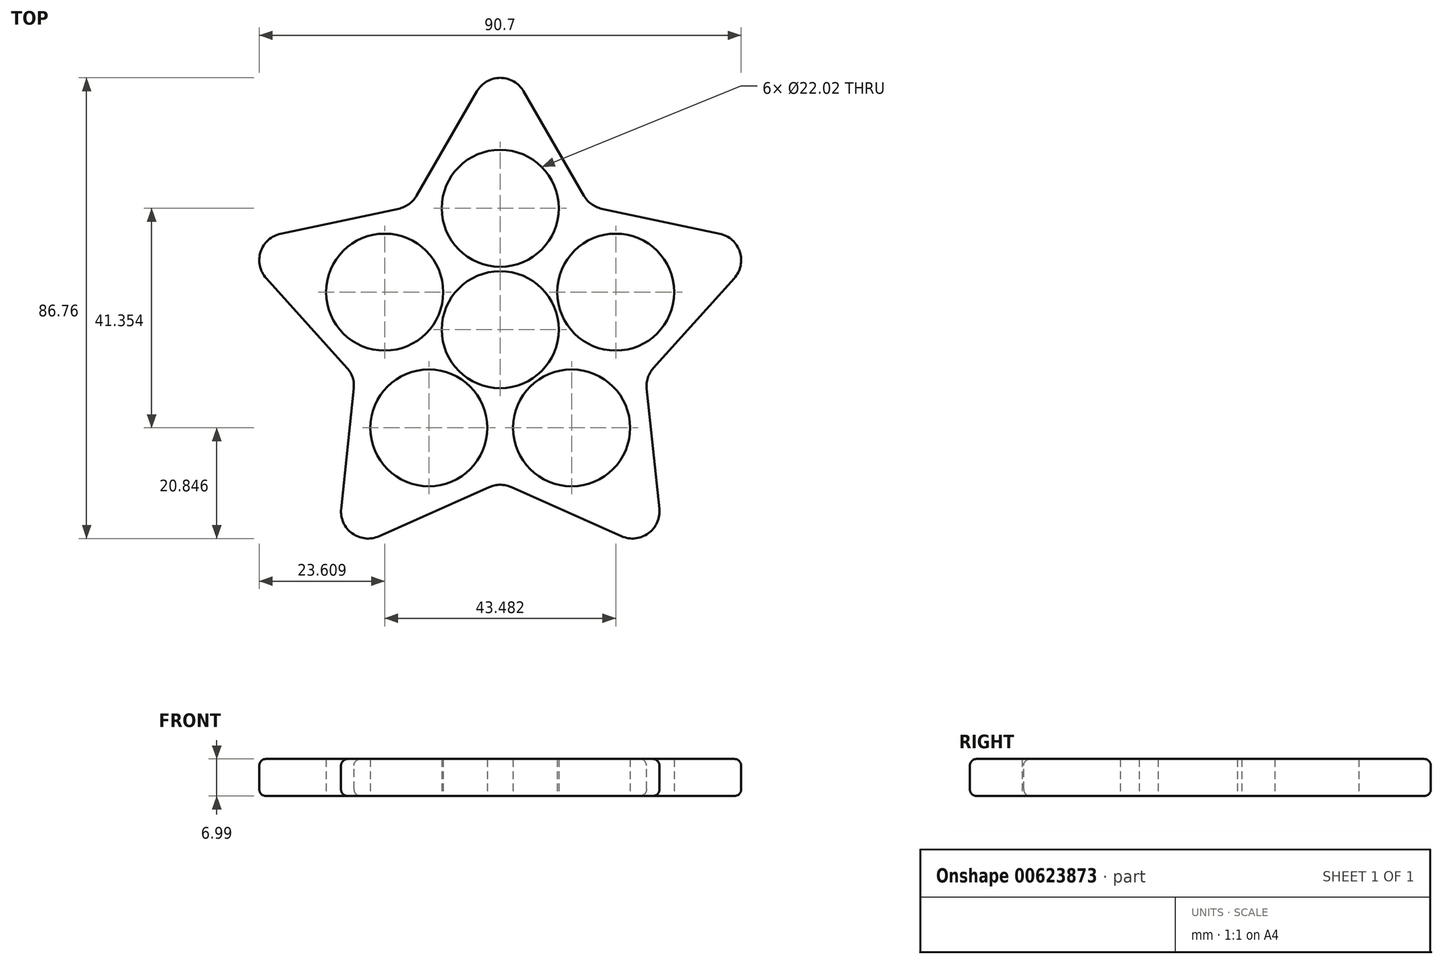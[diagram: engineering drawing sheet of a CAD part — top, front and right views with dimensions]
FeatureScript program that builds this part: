
annotation { "Feature Type Name" : "Feature", "Feature Type Description" : "" }
export const myFeature = defineFeature(function(context is Context, id is Id, definition is map)
    precondition{}
    {
        {
            var Q0;
            Q0=qCreatedBy(makeId("Top.planeOp"),FACE);
            var sketch = newSketch(context, id + "F0", { "sketchPlane" : qUnion([Q0])});
            skCircle(sketch, "E0", {"center": v(0, 0) * mm, "radius": 11.01 * mm});
            skCircle(sketch, "E1", {"center": v(0, 22.86) * mm, "radius": 11.01 * mm});
            skLineSegment(sketch, "E2", {"start": v(0, 22.86) * mm, "end": v(0, 0) * mm});
            skCircle(sketch, "E3.cCircle", {"center": v(0, 22.86) * mm, "radius": 29.64 * mm, "construction": true});
            skLineSegment(sketch, "E3.0", {"start": v(25.67, 8.04) * mm, "end": v(-25.67, 8.04) * mm});
            skLineSegment(sketch, "E3.1", {"start": v(-25.67, 8.04) * mm, "end": v(0, 52.5) * mm});
            skLineSegment(sketch, "E3.2", {"start": v(0, 52.5) * mm, "end": v(25.67, 8.04) * mm});
            skLineSegment(sketch, "E4.1.0", {"start": v(-49.93, 16.22) * mm, "end": v(0.29, 26.9) * mm});
            skCircle(sketch, "E4.1.1", {"center": v(-21.74, 7.06) * mm, "radius": 29.64 * mm, "construction": true});
            skLineSegment(sketch, "E4.1.2", {"start": v(0.29, 26.9) * mm, "end": v(-15.58, -21.93) * mm});
            skLineSegment(sketch, "E4.1.3", {"start": v(-21.74, 7.06) * mm, "end": v(0, 0) * mm});
            skCircle(sketch, "E4.1.4", {"center": v(-21.74, 7.06) * mm, "radius": 11.01 * mm});
            skLineSegment(sketch, "E4.1.5", {"start": v(-15.58, -21.93) * mm, "end": v(-49.93, 16.22) * mm});
            skLineSegment(sketch, "E4.2.0", {"start": v(-30.86, -42.47) * mm, "end": v(-25.5, 8.59) * mm});
            skCircle(sketch, "E4.2.1", {"center": v(-13.44, -18.5) * mm, "radius": 29.64 * mm, "construction": true});
            skLineSegment(sketch, "E4.2.2", {"start": v(-25.5, 8.59) * mm, "end": v(16.04, -21.6) * mm});
            skLineSegment(sketch, "E4.2.3", {"start": v(-13.44, -18.5) * mm, "end": v(0, 0) * mm});
            skCircle(sketch, "E4.2.4", {"center": v(-13.44, -18.5) * mm, "radius": 11.01 * mm});
            skLineSegment(sketch, "E4.2.5", {"start": v(16.04, -21.6) * mm, "end": v(-30.86, -42.47) * mm});
            skLineSegment(sketch, "E4.3.0", {"start": v(30.86, -42.47) * mm, "end": v(-16.04, -21.6) * mm});
            skCircle(sketch, "E4.3.1", {"center": v(13.44, -18.5) * mm, "radius": 29.64 * mm, "construction": true});
            skLineSegment(sketch, "E4.3.2", {"start": v(-16.04, -21.6) * mm, "end": v(25.5, 8.59) * mm});
            skLineSegment(sketch, "E4.3.3", {"start": v(13.44, -18.5) * mm, "end": v(0, 0) * mm});
            skCircle(sketch, "E4.3.4", {"center": v(13.44, -18.5) * mm, "radius": 11.01 * mm});
            skLineSegment(sketch, "E4.3.5", {"start": v(25.5, 8.59) * mm, "end": v(30.86, -42.47) * mm});
            skLineSegment(sketch, "E4.4.0", {"start": v(49.93, 16.22) * mm, "end": v(15.58, -21.93) * mm});
            skCircle(sketch, "E4.4.1", {"center": v(21.74, 7.06) * mm, "radius": 29.64 * mm, "construction": true});
            skLineSegment(sketch, "E4.4.2", {"start": v(15.58, -21.93) * mm, "end": v(-0.29, 26.9) * mm});
            skLineSegment(sketch, "E4.4.3", {"start": v(21.74, 7.06) * mm, "end": v(0, 0) * mm});
            skCircle(sketch, "E4.4.4", {"center": v(21.74, 7.06) * mm, "radius": 11.01 * mm});
            skLineSegment(sketch, "E4.4.5", {"start": v(-0.29, 26.9) * mm, "end": v(49.93, 16.22) * mm});
            skSolve(sketch);
        }
        {
            var Q0;
            Q0 = qSketchRegion(id + "F0", true);
            var Q1;
            {var subQ0=sQuery(id+"F0.wireOp",EDGE,"E3.0");var subQ1=sQuery(id+"F0.wireOp",EDGE,"E0");var subQ2=makeQuery(id+"F0.imprint","INTERSECT",VERTEX,{"disambiguationData":[OD(1.0)],"derivedFrom":[subQ1,subQ0]});Q1=makeQuery(id+"F0.imprint","IMPRINT",FACE,{"disambiguationData":[TD([[makeQuery(id+"F0.imprint","IMPRINT",EDGE,{"disambiguationData":[TD([[subQ2,-1.0]])],"derivedFrom":subQ1}),-1.0]])]});}
            var Q2;
            {var subQ0=sQuery(id+"F0.wireOp",EDGE,"E4.1.3");var subQ1=sQuery(id+"F0.wireOp",EDGE,"E0");var subQ2=makeQuery(id+"F0.imprint","INTERSECT",VERTEX,{"derivedFrom":[subQ1,subQ0]});Q2=makeQuery(id+"F0.imprint","IMPRINT",FACE,{"disambiguationData":[TD([[makeQuery(id+"F0.imprint","IMPRINT",EDGE,{"disambiguationData":[TD([[subQ2,-1.0]])],"derivedFrom":subQ1}),-1.0]])]});}
            var Q3;
            {var subQ0=sQuery(id+"F0.wireOp",EDGE,"E4.2.3");var subQ1=sQuery(id+"F0.wireOp",EDGE,"E0");var subQ2=makeQuery(id+"F0.imprint","INTERSECT",VERTEX,{"derivedFrom":[subQ1,subQ0]});Q3=makeQuery(id+"F0.imprint","IMPRINT",FACE,{"disambiguationData":[TD([[makeQuery(id+"F0.imprint","IMPRINT",EDGE,{"disambiguationData":[TD([[subQ2,-1.0]])],"derivedFrom":subQ1}),-1.0]])]});}
            var Q4;
            {var subQ0=sQuery(id+"F0.wireOp",EDGE,"E4.1.2");var subQ1=sQuery(id+"F0.wireOp",EDGE,"E0");var subQ2=makeQuery(id+"F0.imprint","INTERSECT",VERTEX,{"disambiguationData":[OD(1.0)],"derivedFrom":[subQ1,subQ0]});Q4=makeQuery(id+"F0.imprint","IMPRINT",FACE,{"disambiguationData":[TD([[makeQuery(id+"F0.imprint","IMPRINT",EDGE,{"disambiguationData":[TD([[subQ2,-1.0]])],"derivedFrom":subQ1}),-1.0]])]});}
            var Q5;
            {var subQ0=sQuery(id+"F0.wireOp",EDGE,"E4.3.3");var subQ1=sQuery(id+"F0.wireOp",EDGE,"E0");var subQ2=makeQuery(id+"F0.imprint","INTERSECT",VERTEX,{"derivedFrom":[subQ1,subQ0]});Q5=makeQuery(id+"F0.imprint","IMPRINT",FACE,{"disambiguationData":[TD([[makeQuery(id+"F0.imprint","IMPRINT",EDGE,{"disambiguationData":[TD([[subQ2,-1.0]])],"derivedFrom":subQ1}),-1.0]])]});}
            var Q6;
            {var subQ0=sQuery(id+"F0.wireOp",EDGE,"E4.2.2");var subQ1=sQuery(id+"F0.wireOp",EDGE,"E0");var subQ2=makeQuery(id+"F0.imprint","INTERSECT",VERTEX,{"disambiguationData":[OD(1.0)],"derivedFrom":[subQ1,subQ0]});Q6=makeQuery(id+"F0.imprint","IMPRINT",FACE,{"disambiguationData":[TD([[makeQuery(id+"F0.imprint","IMPRINT",EDGE,{"disambiguationData":[TD([[subQ2,-1.0]])],"derivedFrom":subQ1}),-1.0]])]});}
            var Q7;
            {var subQ0=sQuery(id+"F0.wireOp",EDGE,"E4.4.3");var subQ1=sQuery(id+"F0.wireOp",EDGE,"E0");var subQ2=makeQuery(id+"F0.imprint","INTERSECT",VERTEX,{"derivedFrom":[subQ1,subQ0]});Q7=makeQuery(id+"F0.imprint","IMPRINT",FACE,{"disambiguationData":[TD([[makeQuery(id+"F0.imprint","IMPRINT",EDGE,{"disambiguationData":[TD([[subQ2,1.0]])],"derivedFrom":subQ1}),-1.0]])]});}
            var Q8;
            {var subQ0=sQuery(id+"F0.wireOp",EDGE,"E3.0");var subQ1=sQuery(id+"F0.wireOp",EDGE,"E0");var subQ2=makeQuery(id+"F0.imprint","INTERSECT",VERTEX,{"disambiguationData":[OD(0.0)],"derivedFrom":[subQ1,subQ0]});Q8=makeQuery(id+"F0.imprint","IMPRINT",FACE,{"disambiguationData":[TD([[makeQuery(id+"F0.imprint","IMPRINT",EDGE,{"disambiguationData":[TD([[subQ2,1.0]])],"derivedFrom":subQ1}),-1.0]])]});}
            var Q9;
            {var subQ0=sQuery(id+"F0.wireOp",EDGE,"E4.4.2");var subQ1=sQuery(id+"F0.wireOp",EDGE,"E0");var subQ2=makeQuery(id+"F0.imprint","INTERSECT",VERTEX,{"disambiguationData":[OD(0.0)],"derivedFrom":[subQ1,subQ0]});Q9=makeQuery(id+"F0.imprint","IMPRINT",FACE,{"disambiguationData":[TD([[makeQuery(id+"F0.imprint","IMPRINT",EDGE,{"disambiguationData":[TD([[subQ2,-1.0]])],"derivedFrom":subQ1}),-1.0]])]});}
            var Q10;
            {var subQ0=sQuery(id+"F0.wireOp",EDGE,"E2");var subQ1=sQuery(id+"F0.wireOp",EDGE,"E0");var subQ2=makeQuery(id+"F0.imprint","INTERSECT",VERTEX,{"derivedFrom":[subQ1,subQ0]});Q10=makeQuery(id+"F0.imprint","IMPRINT",FACE,{"disambiguationData":[TD([[makeQuery(id+"F0.imprint","IMPRINT",EDGE,{"disambiguationData":[TD([[subQ2,-1.0]])],"derivedFrom":subQ1}),-1.0]])]});}
            extrude(context, id + "F1", {"entities" : qUnion([Q0, Q1, Q2, Q3, Q4, Q5, Q6, Q7, Q8, Q9, Q10]), "depth" : 7 * mm, "offsetDistance" : 25.4 * mm});
        }
        {
            var Q0;
            Q0=makeQuery(id+"F1.opExtrude","SWEPT_EDGE",EDGE,{"disambiguationData":[OSD([sQuery(id+"F0.wireOp",EDGE,"E4.1.0"),sQuery(id+"F0.wireOp",EDGE,"E4.1.5")])]});
            var Q1;
            Q1=makeQuery(id+"F1.opExtrude","SWEPT_EDGE",EDGE,{"disambiguationData":[OSD([sQuery(id+"F0.wireOp",EDGE,"E3.1"),sQuery(id+"F0.wireOp",EDGE,"E3.2")])]});
            var Q2;
            Q2=makeQuery(id+"F1.opExtrude","SWEPT_EDGE",EDGE,{"disambiguationData":[OSD([sQuery(id+"F0.wireOp",EDGE,"E4.4.0"),sQuery(id+"F0.wireOp",EDGE,"E4.4.5")])]});
            var Q3;
            Q3=makeQuery(id+"F1.opExtrude","SWEPT_EDGE",EDGE,{"disambiguationData":[OSD([sQuery(id+"F0.wireOp",EDGE,"E4.3.0"),sQuery(id+"F0.wireOp",EDGE,"E4.3.5")])]});
            var Q4;
            Q4=makeQuery(id+"F1.opExtrude","SWEPT_EDGE",EDGE,{"disambiguationData":[OSD([sQuery(id+"F0.wireOp",EDGE,"E4.2.0"),sQuery(id+"F0.wireOp",EDGE,"E4.2.5")])]});
            fillet(context, id + "F2", {"entities" : qUnion([Q0, Q1, Q2, Q3, Q4]), "radius" : 5.08 * mm, "tangentPropagation" : true, "allowEdgeOverflow" : false});
        }
        {
            var Q0;
            Q0=makeQuery(id+"F1.opExtrude","SWEPT_EDGE",EDGE,{"disambiguationData":[OSD([sQuery(id+"F0.wireOp",EDGE,"E3.1"),sQuery(id+"F0.wireOp",EDGE,"E4.1.0")])]});
            var Q1;
            Q1=makeQuery(id+"F1.opExtrude","SWEPT_EDGE",EDGE,{"disambiguationData":[OSD([sQuery(id+"F0.wireOp",EDGE,"E3.2"),sQuery(id+"F0.wireOp",EDGE,"E4.4.5")])]});
            var Q2;
            Q2=makeQuery(id+"F1.opExtrude","SWEPT_EDGE",EDGE,{"disambiguationData":[OSD([sQuery(id+"F0.wireOp",EDGE,"E4.3.5"),sQuery(id+"F0.wireOp",EDGE,"E4.4.0")])]});
            var Q3;
            Q3=makeQuery(id+"F1.opExtrude","SWEPT_EDGE",EDGE,{"disambiguationData":[OSD([sQuery(id+"F0.wireOp",EDGE,"E4.2.5"),sQuery(id+"F0.wireOp",EDGE,"E4.3.0")])]});
            var Q4;
            Q4=makeQuery(id+"F1.opExtrude","SWEPT_EDGE",EDGE,{"disambiguationData":[OSD([sQuery(id+"F0.wireOp",EDGE,"E4.1.5"),sQuery(id+"F0.wireOp",EDGE,"E4.2.0")])]});
            fillet(context, id + "F3", {"entities" : qUnion([Q0, Q1, Q2, Q3, Q4]), "radius" : 5.08 * mm, "tangentPropagation" : true, "allowEdgeOverflow" : false});
        }
        {
            var Q0;
            Q0=makeQuery(id+"F1.opExtrude","CAP_EDGE",EDGE,{"disambiguationData":[OSD([sQuery(id+"F0.wireOp",EDGE,"E4.3.0")])],"isStart":true});
            fillet(context, id + "F4", {"entities" : qUnion([Q0]), "radius" : 1.27 * mm, "tangentPropagation" : true, "allowEdgeOverflow" : false});
        }
        {
            var Q0;
            Q0=makeQuery(id+"F1.opExtrude","CAP_EDGE",EDGE,{"disambiguationData":[OSD([sQuery(id+"F0.wireOp",EDGE,"E3.1")])],"isStart":false});
            fillet(context, id + "F5", {"entities" : qUnion([Q0]), "radius" : 1.27 * mm, "tangentPropagation" : true, "allowEdgeOverflow" : false});
        }
    });
